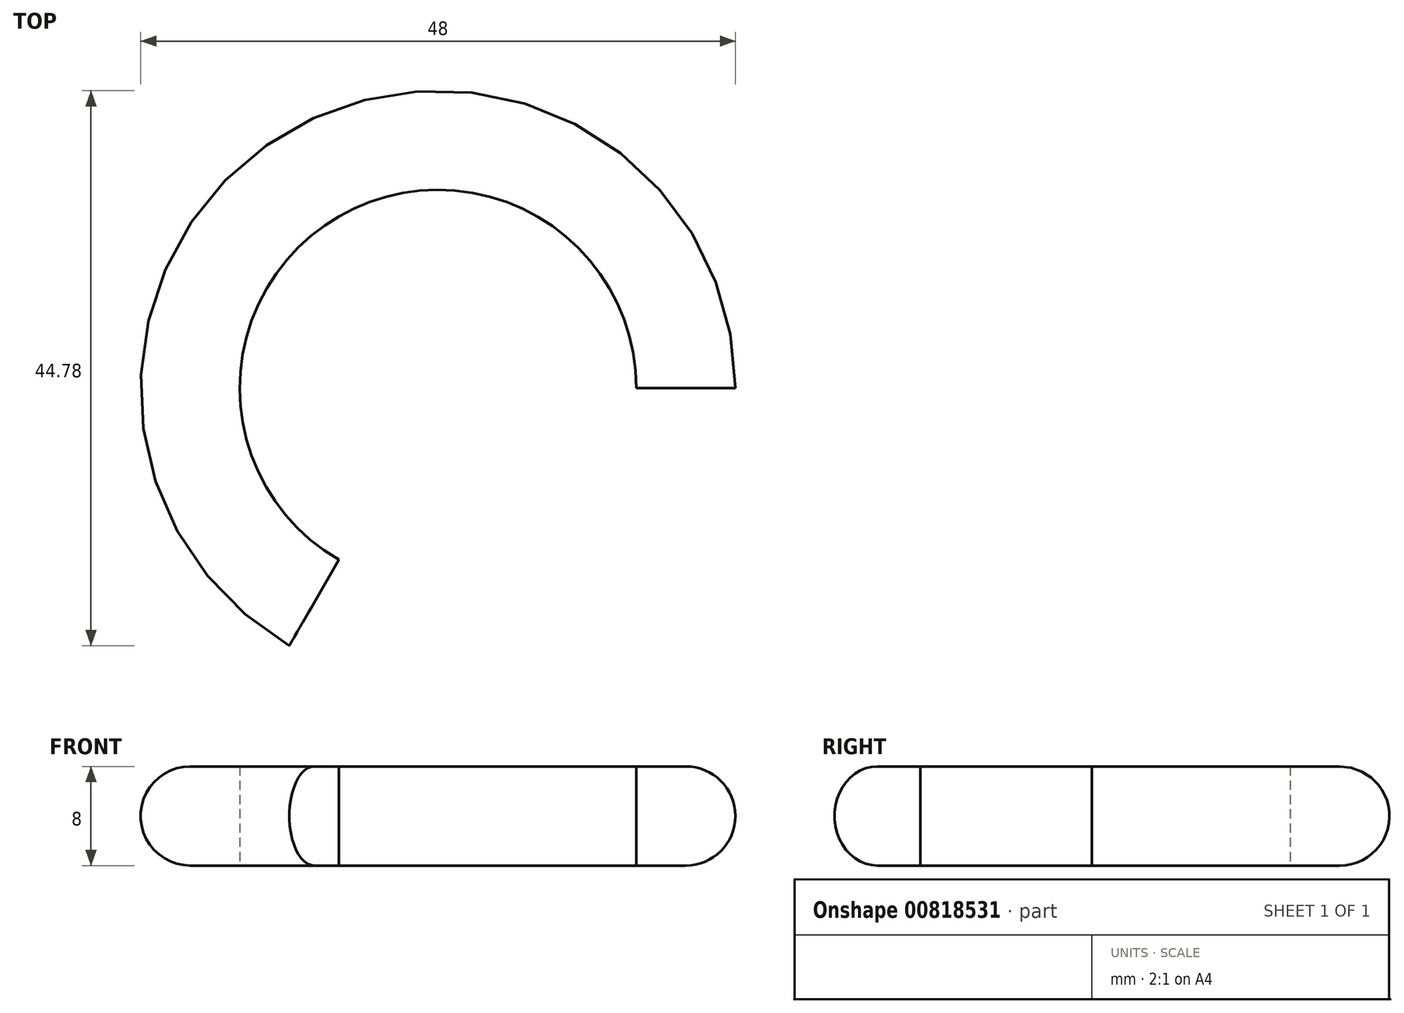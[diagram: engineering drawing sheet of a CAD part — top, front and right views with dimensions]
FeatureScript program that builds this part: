
annotation { "Feature Type Name" : "Feature", "Feature Type Description" : "" }
export const myFeature = defineFeature(function(context is Context, id is Id, definition is map)
    precondition{}
    {
        {
            var Q0;
            Q0=qCreatedBy(makeId("Front.planeOp"),FACE);
            var sketch = newSketch(context, id + "F0", { "sketchPlane" : qUnion([Q0])});
            skLineSegment(sketch, "E0", {"start": v(50.27, 0) * mm, "end": v(34.27, 0) * mm});
            skLineSegment(sketch, "E1", {"start": v(34.27, 0) * mm, "end": v(34.27, 12.83) * mm});
            skLineSegment(sketch, "E2.bottom", {"start": v(50.27, 0) * mm, "end": v(54.27, 0) * mm});
            skLineSegment(sketch, "E2.top", {"start": v(50.27, 8) * mm, "end": v(54.27, 8) * mm});
            skLineSegment(sketch, "E2.left", {"start": v(50.27, 0) * mm, "end": v(50.27, 8) * mm});
            skLineSegment(sketch, "E2.right", {"start": v(54.27, 0) * mm, "end": v(54.27, 8) * mm});
            skArc(sketch, "E3", {"start": v(54.27, 0) * mm, "mid": v(58.27, 4) * mm, "end": v(54.27, 8) * mm});
            skSolve(sketch);
        }
        {
            var Q0;
            Q0=qSketchRegion(id+"F0",true);
            var Q1;
            Q1=sQuery(id+"F0.wireOp",EDGE,"E1");
            revolve(context, id + "F1", {"surfaceOperationType" : NewSurfaceOperationType.NEW, "entities" : qUnion([Q0]), "axis" : qUnion([Q1]), "revolveType" : RevolveType.ONE_DIRECTION, "angle" : 240 * degree});
        }
    });
